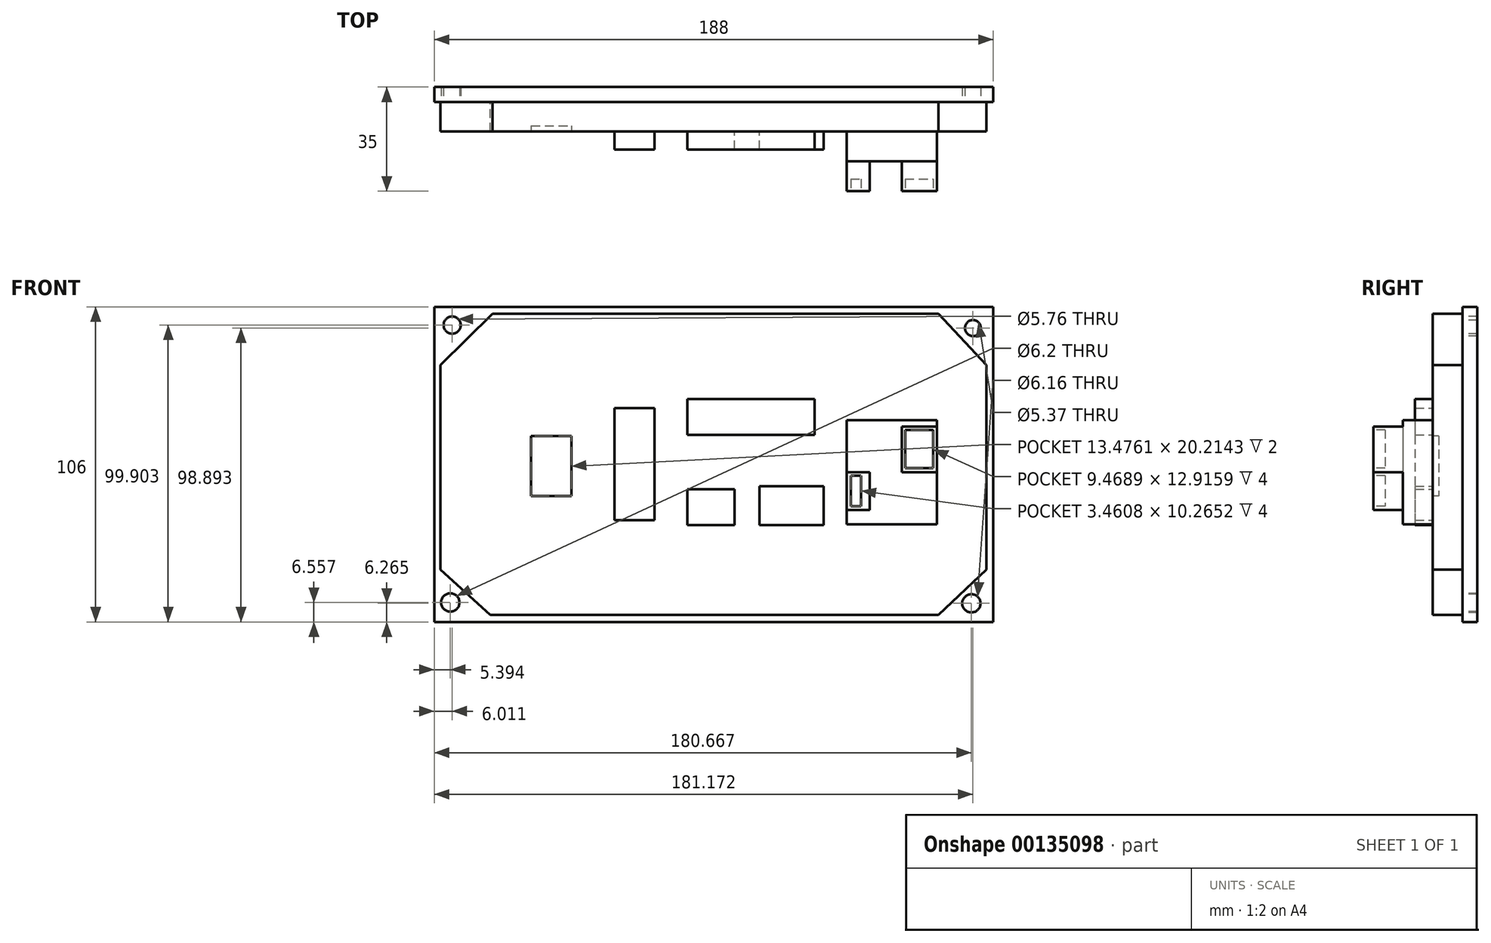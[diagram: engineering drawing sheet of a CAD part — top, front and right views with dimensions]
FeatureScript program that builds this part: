
annotation { "Feature Type Name" : "Feature", "Feature Type Description" : "" }
export const myFeature = defineFeature(function(context is Context, id is Id, definition is map)
    precondition{}
    {
        {
            var Q0;
            Q0=qCreatedBy(makeId("Front.planeOp"),FACE);
            var sketch = newSketch(context, id + "F0", { "sketchPlane" : qUnion([Q0])});
            skLineSegment(sketch, "E0.bottom", {"start": v(-217.04, 129.9) * mm, "end": v(-29.04, 129.9) * mm});
            skLineSegment(sketch, "E0.top", {"start": v(-217.04, 23.9) * mm, "end": v(-29.04, 23.9) * mm});
            skLineSegment(sketch, "E0.left", {"start": v(-217.04, 129.9) * mm, "end": v(-217.04, 23.9) * mm});
            skLineSegment(sketch, "E0.right", {"start": v(-29.04, 129.9) * mm, "end": v(-29.04, 23.9) * mm});
            skSolve(sketch);
        }
        {
            var Q0;
            Q0=makeQuery(id+"F0.imprint","IMPRINT",FACE,{"disambiguationData":[TD([[makeQuery(id+"F0.imprint","IMPRINT",EDGE,{"derivedFrom":sQuery(id+"F0.wireOp",EDGE,"E0.bottom")}),-1.0]])]});
            extrude(context, id + "F1", {"entities" : qUnion([Q0]), "depth" : 5 * mm});
        }
        {
            var Q0;
            Q0=makeQuery(id+"F1.opExtrude","CAP_FACE",FACE,{"disambiguationData":[OSD([sQuery(id+"F0.wireOp",EDGE,"E0.bottom"),sQuery(id+"F0.wireOp",EDGE,"E0.top"),sQuery(id+"F0.wireOp",EDGE,"E0.left"),sQuery(id+"F0.wireOp",EDGE,"E0.right")])],"isStart":false});
            var sketch = newSketch(context, id + "F2", { "sketchPlane" : qUnion([Q0])});
            skLineSegment(sketch, "E1.bottom", {"start": v(-197.39, 127.65) * mm, "end": v(-47.52, 127.65) * mm});
            skLineSegment(sketch, "E1.left", {"start": v(-214.95, 110.37) * mm, "end": v(-214.95, 41.52) * mm});
            skLineSegment(sketch, "E1.right", {"start": v(-31.37, 110.37) * mm, "end": v(-31.37, 41.52) * mm});
            skLineSegment(sketch, "E2", {"start": v(-197.39, 127.65) * mm, "end": v(-214.95, 110.37) * mm});
            skLineSegment(sketch, "E3", {"start": v(-31.37, 110.37) * mm, "end": v(-47.52, 127.65) * mm});
            skLineSegment(sketch, "E4", {"start": v(-47.52, 26.23) * mm, "end": v(-31.37, 41.52) * mm});
            skLineSegment(sketch, "E5", {"start": v(-214.95, 41.52) * mm, "end": v(-198.24, 26.23) * mm});
            skLineSegment(sketch, "E6", {"start": v(-198.24, 26.23) * mm, "end": v(-47.52, 26.23) * mm});
            skSolve(sketch);
        }
        {
            var Q0;
            Q0=makeQuery(id+"F2.imprint","IMPRINT",FACE,{"disambiguationData":[TD([[makeQuery(id+"F2.imprint","IMPRINT",EDGE,{"derivedFrom":sQuery(id+"F2.wireOp",EDGE,"E1.bottom")}),-1.0]])]});
            extrude(context, id + "F3", {"entities" : qUnion([Q0]), "operationType" : NewBodyOperationType.ADD, "depth" : 10 * mm});
        }
        {
            var Q0;
            Q0=makeQuery(id+"F1.opExtrude","CAP_FACE",FACE,{"disambiguationData":[OSD([sQuery(id+"F0.wireOp",EDGE,"E0.bottom"),sQuery(id+"F0.wireOp",EDGE,"E0.top"),sQuery(id+"F0.wireOp",EDGE,"E0.left"),sQuery(id+"F0.wireOp",EDGE,"E0.right")])],"isStart":false});
            var sketch = newSketch(context, id + "F4", { "sketchPlane" : qUnion([Q0])});
            skCircle(sketch, "E7", {"center": v(-211.65, 30.46) * mm, "radius": 3.1 * mm});
            skCircle(sketch, "E8", {"center": v(-36.37, 30.16) * mm, "radius": 3.08 * mm});
            skCircle(sketch, "E9", {"center": v(-35.87, 122.8) * mm, "radius": 2.68 * mm});
            skCircle(sketch, "E10", {"center": v(-211.03, 123.8) * mm, "radius": 2.88 * mm});
            skSolve(sketch);
        }
        {
            var Q0;
            Q0=makeQuery(id+"F4.imprint","IMPRINT",FACE,{"disambiguationData":[TD([[makeQuery(id+"F4.imprint","IMPRINT",EDGE,{"derivedFrom":sQuery(id+"F4.wireOp",EDGE,"E10")}),1.0]])]});
            var Q1;
            Q1=makeQuery(id+"F4.imprint","IMPRINT",FACE,{"disambiguationData":[TD([[makeQuery(id+"F4.imprint","IMPRINT",EDGE,{"derivedFrom":sQuery(id+"F4.wireOp",EDGE,"E7")}),1.0]])]});
            var Q2;
            Q2=makeQuery(id+"F4.imprint","IMPRINT",FACE,{"disambiguationData":[TD([[makeQuery(id+"F4.imprint","IMPRINT",EDGE,{"derivedFrom":sQuery(id+"F4.wireOp",EDGE,"E8")}),1.0]])]});
            var Q3;
            Q3=makeQuery(id+"F4.imprint","IMPRINT",FACE,{"disambiguationData":[TD([[makeQuery(id+"F4.imprint","IMPRINT",EDGE,{"derivedFrom":sQuery(id+"F4.wireOp",EDGE,"E9")}),1.0]])]});
            var Q4;
            Q4=sQuery(id+"F4.wireOp",EDGE,"E10");
            var Q5;
            Q5=sQuery(id+"F4.wireOp",EDGE,"E7");
            var Q6;
            Q6=sQuery(id+"F4.wireOp",EDGE,"E8");
            var Q7;
            Q7=sQuery(id+"F4.wireOp",EDGE,"E9");
            extrude(context, id + "F5", {"entities" : qUnion([Q0, Q1, Q2, Q3]), "operationType" : NewBodyOperationType.REMOVE, "surfaceEntities" : qUnion([Q4, Q5, Q6, Q7]), "oppositeDirection" : true, "depth" : 25 * mm});
        }
        {
            var Q0;
            Q0=makeQuery(id+"F3.opExtrude","CAP_FACE",FACE,{"disambiguationData":[OSD([sQuery(id+"F2.wireOp",EDGE,"E1.bottom"),sQuery(id+"F2.wireOp",EDGE,"E1.left"),sQuery(id+"F2.wireOp",EDGE,"E1.right"),sQuery(id+"F2.wireOp",EDGE,"E2"),sQuery(id+"F2.wireOp",EDGE,"E3"),sQuery(id+"F2.wireOp",EDGE,"E4"),sQuery(id+"F2.wireOp",EDGE,"E5"),sQuery(id+"F2.wireOp",EDGE,"E6")])],"isStart":false});
            var sketch = newSketch(context, id + "F6", { "sketchPlane" : qUnion([Q0])});
            skLineSegment(sketch, "E11.bottom", {"start": v(-184.43, 86.45) * mm, "end": v(-170.96, 86.45) * mm});
            skLineSegment(sketch, "E11.top", {"start": v(-184.43, 66.24) * mm, "end": v(-170.96, 66.24) * mm});
            skLineSegment(sketch, "E11.left", {"start": v(-184.43, 86.45) * mm, "end": v(-184.43, 66.24) * mm});
            skLineSegment(sketch, "E11.right", {"start": v(-170.96, 86.45) * mm, "end": v(-170.96, 66.24) * mm});
            skLineSegment(sketch, "E12.bottom", {"start": v(-78.3, 91.84) * mm, "end": v(-47.99, 91.84) * mm});
            skLineSegment(sketch, "E12.top", {"start": v(-78.3, 56.8) * mm, "end": v(-47.99, 56.8) * mm});
            skLineSegment(sketch, "E12.left", {"start": v(-78.3, 91.84) * mm, "end": v(-78.3, 56.8) * mm});
            skLineSegment(sketch, "E12.right", {"start": v(-47.99, 91.84) * mm, "end": v(-47.99, 56.8) * mm});
            skLineSegment(sketch, "E13.bottom", {"start": v(-156.47, 95.89) * mm, "end": v(-143, 95.89) * mm});
            skLineSegment(sketch, "E13.top", {"start": v(-156.47, 58.15) * mm, "end": v(-143, 58.15) * mm});
            skLineSegment(sketch, "E13.left", {"start": v(-156.47, 95.89) * mm, "end": v(-156.47, 58.15) * mm});
            skLineSegment(sketch, "E13.right", {"start": v(-143, 95.89) * mm, "end": v(-143, 58.15) * mm});
            skLineSegment(sketch, "E14.bottom", {"start": v(-131.88, 98.92) * mm, "end": v(-124.8, 98.92) * mm});
            skLineSegment(sketch, "E14.left", {"start": v(-131.88, 98.92) * mm, "end": v(-131.88, 94.54) * mm});
            skLineSegment(sketch, "E15.bottom", {"start": v(-131.88, 68.6) * mm, "end": v(-116.04, 68.6) * mm});
            skLineSegment(sketch, "E15.top", {"start": v(-131.88, 56.47) * mm, "end": v(-116.04, 56.47) * mm});
            skLineSegment(sketch, "E15.left", {"start": v(-131.88, 68.6) * mm, "end": v(-131.88, 56.47) * mm});
            skLineSegment(sketch, "E15.right", {"start": v(-116.04, 68.6) * mm, "end": v(-116.04, 56.47) * mm});
            skLineSegment(sketch, "E16.bottom", {"start": v(-107.62, 69.6) * mm, "end": v(-86.06, 69.6) * mm});
            skLineSegment(sketch, "E16.top", {"start": v(-107.62, 56.47) * mm, "end": v(-86.06, 56.47) * mm});
            skLineSegment(sketch, "E16.left", {"start": v(-107.62, 69.6) * mm, "end": v(-107.62, 56.47) * mm});
            skLineSegment(sketch, "E16.right", {"start": v(-86.06, 69.6) * mm, "end": v(-86.06, 56.47) * mm});
            skLineSegment(sketch, "E17.bottom", {"start": v(-131.88, 98.92) * mm, "end": v(-89.09, 98.92) * mm});
            skLineSegment(sketch, "E17.top", {"start": v(-131.88, 86.79) * mm, "end": v(-89.09, 86.79) * mm});
            skLineSegment(sketch, "E17.left", {"start": v(-131.88, 98.92) * mm, "end": v(-131.88, 86.79) * mm});
            skLineSegment(sketch, "E17.right", {"start": v(-89.09, 98.92) * mm, "end": v(-89.09, 86.79) * mm});
            skSolve(sketch);
        }
        {
            var Q0;
            Q0=makeQuery(id+"F6.imprint","IMPRINT",FACE,{"disambiguationData":[TD([[makeQuery(id+"F6.imprint","IMPRINT",EDGE,{"derivedFrom":sQuery(id+"F6.wireOp",EDGE,"E11.bottom")}),-1.0]])]});
            extrude(context, id + "F7", {"entities" : qUnion([Q0]), "operationType" : NewBodyOperationType.REMOVE, "oppositeDirection" : true, "depth" : 2 * mm});
        }
        {
            var Q0;
            Q0=makeQuery(id+"F6.imprint","IMPRINT",FACE,{"disambiguationData":[TD([[makeQuery(id+"F6.imprint","IMPRINT",EDGE,{"derivedFrom":sQuery(id+"F6.wireOp",EDGE,"E13.bottom")}),-1.0]])]});
            var Q1;
            {var subQ5=sQuery(id+"F6.wireOp",EDGE,"E17.top");Q1=makeQuery(id+"F6.imprint","IMPRINT",FACE,{"disambiguationData":[TD([[makeQuery(id+"F6.imprint","IMPRINT",EDGE,{"derivedFrom":subQ5}),1.0]])]});}
            var Q2;
            Q2=makeQuery(id+"F6.imprint","IMPRINT",FACE,{"disambiguationData":[TD([[makeQuery(id+"F6.imprint","IMPRINT",EDGE,{"derivedFrom":sQuery(id+"F6.wireOp",EDGE,"E15.bottom")}),-1.0]])]});
            var Q3;
            Q3=makeQuery(id+"F6.imprint","IMPRINT",FACE,{"disambiguationData":[TD([[makeQuery(id+"F6.imprint","IMPRINT",EDGE,{"derivedFrom":sQuery(id+"F6.wireOp",EDGE,"E16.bottom")}),-1.0]])]});
            extrude(context, id + "F8", {"entities" : qUnion([Q0, Q1, Q2, Q3]), "operationType" : NewBodyOperationType.ADD, "depth" : 6 * mm});
        }
        {
            var Q0;
            Q0=makeQuery(id+"F6.imprint","IMPRINT",FACE,{"disambiguationData":[TD([[makeQuery(id+"F6.imprint","IMPRINT",EDGE,{"derivedFrom":sQuery(id+"F6.wireOp",EDGE,"E12.bottom")}),-1.0]])]});
            extrude(context, id + "F9", {"entities" : qUnion([Q0]), "operationType" : NewBodyOperationType.ADD, "depth" : 10 * mm});
        }
        {
            var Q0;
            Q0=makeQuery(id+"F9.opExtrude","CAP_FACE",FACE,{"disambiguationData":[OSD([sQuery(id+"F6.wireOp",EDGE,"E12.bottom"),sQuery(id+"F6.wireOp",EDGE,"E12.top"),sQuery(id+"F6.wireOp",EDGE,"E12.left"),sQuery(id+"F6.wireOp",EDGE,"E12.right")])],"isStart":false});
            var sketch = newSketch(context, id + "F10", { "sketchPlane" : qUnion([Q0])});
            skLineSegment(sketch, "E18.bottom", {"start": v(-59.82, 89.7) * mm, "end": v(-47.99, 89.7) * mm});
            skLineSegment(sketch, "E18.top", {"start": v(-59.82, 74.32) * mm, "end": v(-47.99, 74.32) * mm});
            skLineSegment(sketch, "E18.left", {"start": v(-59.82, 89.7) * mm, "end": v(-59.82, 74.32) * mm});
            skLineSegment(sketch, "E18.right", {"start": v(-47.99, 89.7) * mm, "end": v(-47.99, 74.32) * mm});
            skLineSegment(sketch, "E19.bottom", {"start": v(-78.3, 74.32) * mm, "end": v(-70.6, 74.32) * mm});
            skLineSegment(sketch, "E19.top", {"start": v(-78.3, 61.52) * mm, "end": v(-70.6, 61.52) * mm});
            skLineSegment(sketch, "E19.left", {"start": v(-78.3, 74.32) * mm, "end": v(-78.3, 61.52) * mm});
            skLineSegment(sketch, "E19.right", {"start": v(-70.6, 74.32) * mm, "end": v(-70.6, 61.52) * mm});
            skSolve(sketch);
        }
        {
            var Q0;
            Q0=makeQuery(id+"F10.imprint","IMPRINT",FACE,{"disambiguationData":[TD([[makeQuery(id+"F10.imprint","IMPRINT",EDGE,{"derivedFrom":sQuery(id+"F10.wireOp",EDGE,"E18.bottom")}),-1.0]])]});
            var Q1;
            Q1=makeQuery(id+"F10.imprint","IMPRINT",FACE,{"disambiguationData":[TD([[makeQuery(id+"F10.imprint","IMPRINT",EDGE,{"derivedFrom":sQuery(id+"F10.wireOp",EDGE,"E19.bottom")}),-1.0]])]});
            extrude(context, id + "F11", {"entities" : qUnion([Q0, Q1]), "operationType" : NewBodyOperationType.ADD, "depth" : 10 * mm});
        }
        {
            var Q0;
            Q0=makeQuery(id+"F11.opExtrude","CAP_FACE",FACE,{"disambiguationData":[OSD([sQuery(id+"F10.wireOp",EDGE,"E18.bottom"),sQuery(id+"F10.wireOp",EDGE,"E18.top"),sQuery(id+"F10.wireOp",EDGE,"E18.left"),sQuery(id+"F10.wireOp",EDGE,"E18.right")])],"isStart":false});
            var sketch = newSketch(context, id + "F12", { "sketchPlane" : qUnion([Q0])});
            skLineSegment(sketch, "E20.bottom", {"start": v(-58.67, 88.54) * mm, "end": v(-49.2, 88.54) * mm});
            skLineSegment(sketch, "E20.top", {"start": v(-58.67, 75.63) * mm, "end": v(-49.2, 75.63) * mm});
            skLineSegment(sketch, "E20.left", {"start": v(-58.67, 88.54) * mm, "end": v(-58.67, 75.63) * mm});
            skLineSegment(sketch, "E20.right", {"start": v(-49.2, 88.54) * mm, "end": v(-49.2, 75.63) * mm});
            skSolve(sketch);
        }
        {
            var Q0;
            Q0=makeQuery(id+"F12.imprint","IMPRINT",FACE,{"disambiguationData":[TD([[makeQuery(id+"F12.imprint","IMPRINT",EDGE,{"derivedFrom":sQuery(id+"F12.wireOp",EDGE,"E20.bottom")}),-1.0]])]});
            extrude(context, id + "F13", {"entities" : qUnion([Q0]), "operationType" : NewBodyOperationType.REMOVE, "oppositeDirection" : true, "depth" : 4 * mm});
        }
        {
            var Q0;
            Q0=makeQuery(id+"F11.opExtrude","CAP_FACE",FACE,{"disambiguationData":[OSD([sQuery(id+"F10.wireOp",EDGE,"E19.bottom"),sQuery(id+"F10.wireOp",EDGE,"E19.top"),sQuery(id+"F10.wireOp",EDGE,"E19.left"),sQuery(id+"F10.wireOp",EDGE,"E19.right")])],"isStart":false});
            var sketch = newSketch(context, id + "F14", { "sketchPlane" : qUnion([Q0])});
            skLineSegment(sketch, "E21.bottom", {"start": v(-76.95, 73.16) * mm, "end": v(-73.5, 73.16) * mm});
            skLineSegment(sketch, "E21.top", {"start": v(-76.95, 62.9) * mm, "end": v(-73.5, 62.9) * mm});
            skLineSegment(sketch, "E21.left", {"start": v(-76.95, 73.16) * mm, "end": v(-76.95, 62.9) * mm});
            skLineSegment(sketch, "E21.right", {"start": v(-73.5, 73.16) * mm, "end": v(-73.5, 62.9) * mm});
            skSolve(sketch);
        }
        {
            var Q0;
            Q0=makeQuery(id+"F14.imprint","IMPRINT",FACE,{"disambiguationData":[TD([[makeQuery(id+"F14.imprint","IMPRINT",EDGE,{"derivedFrom":sQuery(id+"F14.wireOp",EDGE,"E21.bottom")}),-1.0]])]});
            extrude(context, id + "F15", {"entities" : qUnion([Q0]), "operationType" : NewBodyOperationType.REMOVE, "oppositeDirection" : true, "depth" : 4 * mm});
        }
    });
